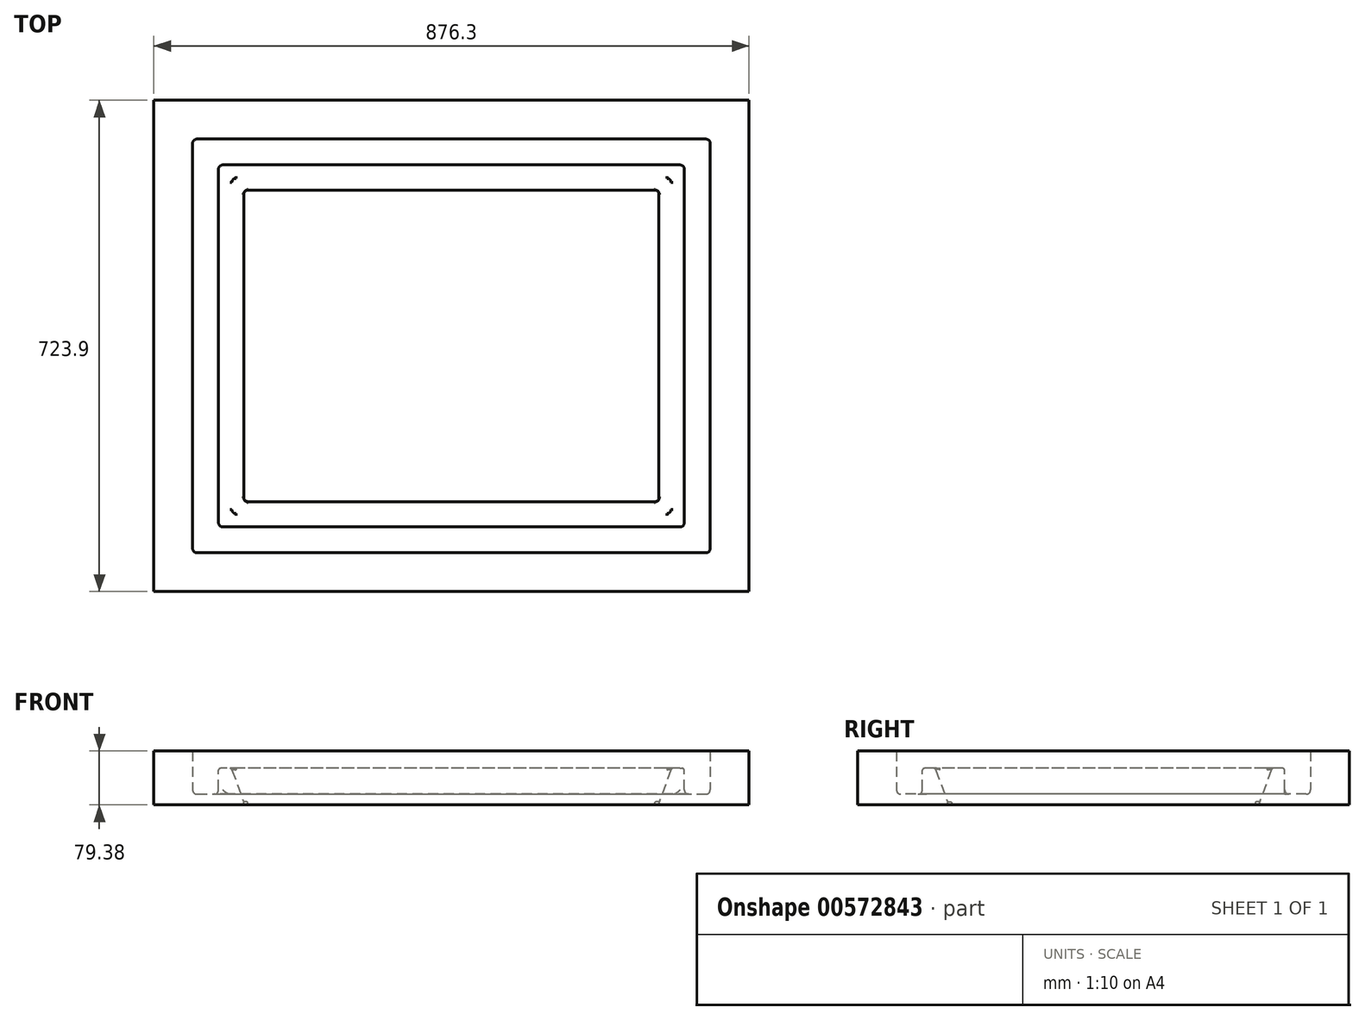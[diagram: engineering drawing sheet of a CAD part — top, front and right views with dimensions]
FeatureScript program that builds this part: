
annotation { "Feature Type Name" : "Feature", "Feature Type Description" : "" }
export const myFeature = defineFeature(function(context is Context, id is Id, definition is map)
    precondition{}
    {
        {
            var Q0;
            Q0=qCreatedBy(makeId("Top.planeOp"),FACE);
            var sketch = newSketch(context, id + "F0", { "sketchPlane" : qUnion([Q0])});
            skLineSegment(sketch, "E0.bottom", {"start": v(-381, 304.8) * mm, "end": v(381, 304.8) * mm});
            skLineSegment(sketch, "E0.top", {"start": v(-381, -304.8) * mm, "end": v(381, -304.8) * mm});
            skLineSegment(sketch, "E0.left", {"start": v(-381, 304.8) * mm, "end": v(-381, -304.8) * mm});
            skLineSegment(sketch, "E0.right", {"start": v(381, 304.8) * mm, "end": v(381, -304.8) * mm});
            skSolve(sketch);
        }
        {
            var Q0;
            Q0=qCreatedBy(makeId("Front.planeOp"),FACE);
            var sketch = newSketch(context, id + "F1", { "sketchPlane" : qUnion([Q0])});
            skLineSegment(sketch, "E1.0", {"start": v(-381, 0) * mm, "end": v(381, 0) * mm});
            skLineSegment(sketch, "E2", {"start": v(-381, 0) * mm, "end": v(-381, -63.5) * mm});
            skLineSegment(sketch, "E3", {"start": v(-381, -63.5) * mm, "end": v(-342.9, -63.5) * mm});
            skLineSegment(sketch, "E4", {"start": v(-342.9, -63.5) * mm, "end": v(-342.9, -25.4) * mm});
            skLineSegment(sketch, "E5", {"start": v(-342.9, -25.4) * mm, "end": v(-323.85, -25.4) * mm});
            skLineSegment(sketch, "E6", {"start": v(-323.85, -25.4) * mm, "end": v(-304.2, -79.38) * mm});
            skLineSegment(sketch, "E7", {"start": v(-438.15, -79.38) * mm, "end": v(-304.2, -79.38) * mm});
            skLineSegment(sketch, "E8", {"start": v(-438.15, -79.38) * mm, "end": v(-438.15, 0) * mm});
            skLineSegment(sketch, "E9", {"start": v(-438.15, 0) * mm, "end": v(-381, 0) * mm});
            skSolve(sketch);
        }
        {
            var Q0;
            Q0=makeQuery(id+"F1.imprint","IMPRINT",FACE,{"disambiguationData":[TD([[makeQuery(id+"F1.imprint","IMPRINT",EDGE,{"derivedFrom":sQuery(id+"F1.wireOp",EDGE,"E2")}),-1.0]])]});
            var Q1;
            Q1=sQuery(id+"F0.wireOp",EDGE,"E0.left");
            var Q2;
            Q2=sQuery(id+"F0.wireOp",EDGE,"E0.top");
            var Q3;
            Q3=sQuery(id+"F0.wireOp",EDGE,"E0.right");
            var Q4;
            Q4=sQuery(id+"F0.wireOp",EDGE,"E0.bottom");
            sweep(context, id + "F2", {"profiles" : qUnion([Q0]), "path" : qUnion([Q1, Q2, Q3, Q4])});
        }
        {
            var Q0;
            Q0=makeQuery(id+"F2.opSweep","SWEPT_EDGE",EDGE,{"disambiguationData":[OSD([sQuery(id+"F0.wireOp",EDGE,"E0.left"),sQuery(id+"F1.wireOp",EDGE,"E2"),sQuery(id+"F1.wireOp",EDGE,"E3")])]});
            var Q1;
            Q1=makeQuery(id+"F2.opSweep","SWEPT_EDGE",EDGE,{"disambiguationData":[OSD([sQuery(id+"F0.wireOp",EDGE,"E0.bottom"),sQuery(id+"F1.wireOp",EDGE,"E2"),sQuery(id+"F1.wireOp",EDGE,"E3")])]});
            var Q2;
            Q2=makeQuery(id+"F2.opSweep","SWEPT_EDGE",EDGE,{"disambiguationData":[OSD([sQuery(id+"F0.wireOp",EDGE,"E0.right"),sQuery(id+"F1.wireOp",EDGE,"E2"),sQuery(id+"F1.wireOp",EDGE,"E3")])]});
            var Q3;
            Q3=makeQuery(id+"F2.opSweep","SWEPT_EDGE",EDGE,{"disambiguationData":[OSD([sQuery(id+"F0.wireOp",EDGE,"E0.top"),sQuery(id+"F1.wireOp",EDGE,"E2"),sQuery(id+"F1.wireOp",EDGE,"E3")])]});
            var Q4;
            Q4=makeQuery(id+"F2.opSweep","SWEPT_EDGE",EDGE,{"disambiguationData":[OSD([sQuery(id+"F0.wireOp",EDGE,"E0.top"),sQuery(id+"F1.wireOp",EDGE,"E3"),sQuery(id+"F1.wireOp",EDGE,"E4")])]});
            var Q5;
            Q5=makeQuery(id+"F2.opSweep","MID_CAP_EDGE",EDGE,{"disambiguationData":[OSD([sQuery(id+"F0.wireOp",VERTEX,"E0.top.start"),sQuery(id+"F1.wireOp",EDGE,"E4")])],"capPos":1.0});
            var Q6;
            Q6=makeQuery(id+"F2.opSweep","SWEPT_EDGE",EDGE,{"disambiguationData":[OSD([sQuery(id+"F0.wireOp",EDGE,"E0.left"),sQuery(id+"F1.wireOp",EDGE,"E3"),sQuery(id+"F1.wireOp",EDGE,"E4")])]});
            var Q7;
            Q7=makeQuery(id+"F2.opSweep","MID_CAP_EDGE",EDGE,{"disambiguationData":[OSD([sQuery(id+"F0.wireOp",VERTEX,"E0.top.start"),sQuery(id+"F1.wireOp",EDGE,"E2")])],"capPos":1.0});
            var Q8;
            Q8=makeQuery(id+"F2.opSweep","CAP_EDGE",EDGE,{"disambiguationData":[OSD([sQuery(id+"F0.wireOp",VERTEX,"E0.bottom.start"),sQuery(id+"F1.wireOp",EDGE,"E2")])],"isStart":true});
            var Q9;
            Q9=makeQuery(id+"F2.opSweep","CAP_EDGE",EDGE,{"disambiguationData":[OSD([sQuery(id+"F0.wireOp",VERTEX,"E0.bottom.start"),sQuery(id+"F1.wireOp",EDGE,"E4")])],"isStart":true});
            var Q10;
            Q10=makeQuery(id+"F2.opSweep","CAP_EDGE",EDGE,{"disambiguationData":[OSD([sQuery(id+"F0.wireOp",VERTEX,"E0.bottom.start"),sQuery(id+"F1.wireOp",EDGE,"E6")])],"isStart":true});
            var Q11;
            Q11=makeQuery(id+"F2.opSweep","SWEPT_EDGE",EDGE,{"disambiguationData":[OSD([sQuery(id+"F0.wireOp",EDGE,"E0.right"),sQuery(id+"F1.wireOp",EDGE,"E3"),sQuery(id+"F1.wireOp",EDGE,"E4")])]});
            var Q12;
            Q12=makeQuery(id+"F2.opSweep","MID_CAP_EDGE",EDGE,{"disambiguationData":[OSD([sQuery(id+"F0.wireOp",VERTEX,"E0.bottom.end"),sQuery(id+"F1.wireOp",EDGE,"E4")])],"capPos":3.0});
            var Q13;
            Q13=makeQuery(id+"F2.opSweep","MID_CAP_EDGE",EDGE,{"disambiguationData":[OSD([sQuery(id+"F0.wireOp",VERTEX,"E0.right.end"),sQuery(id+"F1.wireOp",EDGE,"E4")])],"capPos":2.0});
            var Q14;
            Q14=makeQuery(id+"F2.opSweep","MID_CAP_EDGE",EDGE,{"disambiguationData":[OSD([sQuery(id+"F0.wireOp",VERTEX,"E0.right.end"),sQuery(id+"F1.wireOp",EDGE,"E2")])],"capPos":2.0});
            var Q15;
            Q15=makeQuery(id+"F2.opSweep","MID_CAP_EDGE",EDGE,{"disambiguationData":[OSD([sQuery(id+"F0.wireOp",VERTEX,"E0.top.start"),sQuery(id+"F1.wireOp",EDGE,"E6")])],"capPos":1.0});
            var Q16;
            Q16=makeQuery(id+"F2.opSweep","MID_CAP_EDGE",EDGE,{"disambiguationData":[OSD([sQuery(id+"F0.wireOp",VERTEX,"E0.right.end"),sQuery(id+"F1.wireOp",EDGE,"E6")])],"capPos":2.0});
            var Q17;
            Q17=makeQuery(id+"F2.opSweep","MID_CAP_EDGE",EDGE,{"disambiguationData":[OSD([sQuery(id+"F0.wireOp",VERTEX,"E0.bottom.end"),sQuery(id+"F1.wireOp",EDGE,"E6")])],"capPos":3.0});
            var Q18;
            Q18=makeQuery(id+"F2.opSweep","MID_CAP_EDGE",EDGE,{"disambiguationData":[OSD([sQuery(id+"F0.wireOp",VERTEX,"E0.bottom.end"),sQuery(id+"F1.wireOp",EDGE,"E2")])],"capPos":3.0});
            fillet(context, id + "F3", {"entities" : qUnion([Q0, Q1, Q2, Q3, Q4, Q5, Q6, Q7, Q8, Q9, Q10, Q11, Q12, Q13, Q14, Q15, Q16, Q17, Q18]), "radius" : 6.35 * mm, "tangentPropagation" : true, "allowEdgeOverflow" : false});
        }
        {
            var Q0;
            Q0=makeQuery(id+"F2.opSweep","SWEPT_EDGE",EDGE,{"disambiguationData":[OSD([sQuery(id+"F0.wireOp",EDGE,"E0.left"),sQuery(id+"F1.wireOp",EDGE,"E4"),sQuery(id+"F1.wireOp",EDGE,"E5")])]});
            var Q1;
            Q1=makeQuery(id+"F2.opSweep","SWEPT_EDGE",EDGE,{"disambiguationData":[OSD([sQuery(id+"F0.wireOp",EDGE,"E0.left"),sQuery(id+"F1.wireOp",EDGE,"E5"),sQuery(id+"F1.wireOp",EDGE,"E6")])]});
            fillet(context, id + "F4", {"entities" : qUnion([Q0, Q1]), "radius" : 3.17 * mm, "tangentPropagation" : true, "allowEdgeOverflow" : false});
        }
        {
            var Q0;
            Q0=makeQuery(id+"F2.opSweep","SWEPT_EDGE",EDGE,{"disambiguationData":[OSD([sQuery(id+"F0.wireOp",EDGE,"E0.bottom"),sQuery(id+"F1.wireOp",EDGE,"E6"),sQuery(id+"F1.wireOp",EDGE,"E7")])]});
            fillet(context, id + "F5", {"entities" : qUnion([Q0]), "radius" : 3.17 * mm, "tangentPropagation" : true, "allowEdgeOverflow" : false});
        }
    });
